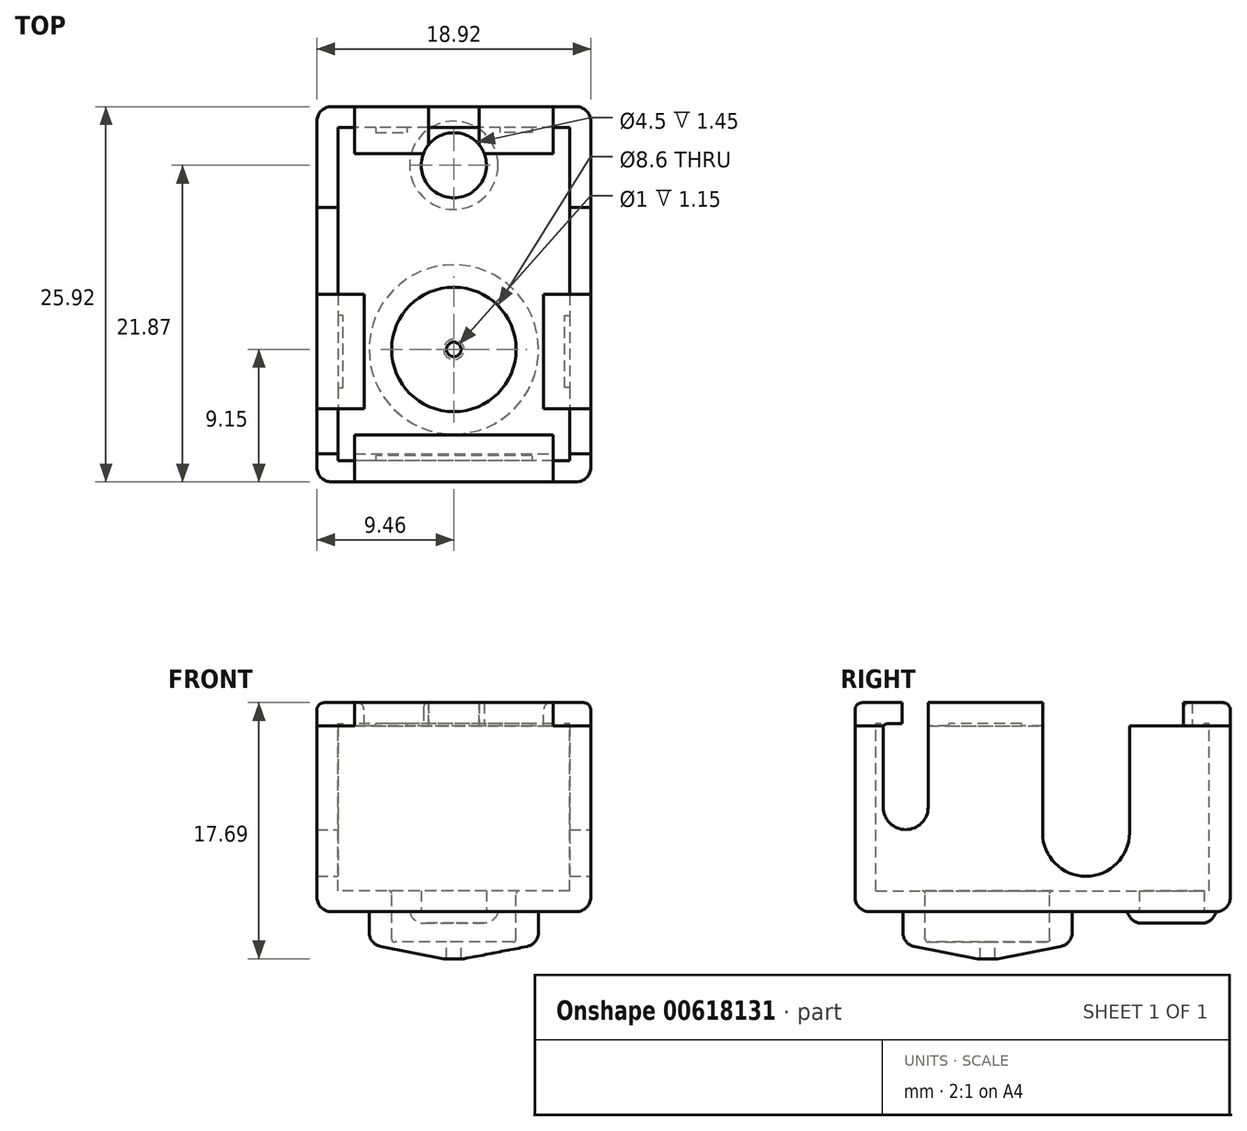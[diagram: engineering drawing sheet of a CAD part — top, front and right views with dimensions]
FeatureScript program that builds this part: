
annotation { "Feature Type Name" : "Feature", "Feature Type Description" : "" }
export const myFeature = defineFeature(function(context is Context, id is Id, definition is map)
    precondition{}
    {
        {
            var Q0;
            Q0=qCreatedBy(makeId("Top.planeOp"),FACE);
            var sketch = newSketch(context, id + "F0", { "sketchPlane" : qUnion([Q0])});
            skLineSegment(sketch, "E0.bottom", {"start": v(9.46, 12.96) * mm, "end": v(-9.45, 12.96) * mm});
            skLineSegment(sketch, "E0.top", {"start": v(9.45, -12.96) * mm, "end": v(-9.46, -12.96) * mm});
            skLineSegment(sketch, "E0.left", {"start": v(9.46, 12.96) * mm, "end": v(9.46, -12.96) * mm});
            skLineSegment(sketch, "E0.right", {"start": v(-9.45, 12.96) * mm, "end": v(-9.46, -12.96) * mm});
            skPoint(sketch, "E0.middle", {"position": v(0, 0) * mm});
            skCircle(sketch, "E1", {"center": v(0, -3.8) * mm, "radius": 5.85 * mm});
            skCircle(sketch, "E2", {"center": v(0, 8.9) * mm, "radius": 3.05 * mm});
            skCircle(sketch, "E3", {"center": v(0, -3.8) * mm, "radius": 4.3 * mm});
            skCircle(sketch, "E4", {"center": v(0, 8.9) * mm, "radius": 2.25 * mm});
            skSolve(sketch);
        }
        {
            var Q0;
            Q0=makeQuery(id+"F0.imprint","IMPRINT",FACE,{"disambiguationData":[TD([[makeQuery(id+"F0.imprint","IMPRINT",EDGE,{"derivedFrom":sQuery(id+"F0.wireOp",EDGE,"E2")}),1.0]])]});
            var Q1;
            Q1=makeQuery(id+"F0.imprint","IMPRINT",FACE,{"disambiguationData":[TD([[makeQuery(id+"F0.imprint","IMPRINT",EDGE,{"derivedFrom":sQuery(id+"F0.wireOp",EDGE,"E0.bottom")}),1.0]])]});
            var Q2;
            Q2=makeQuery(id+"F0.imprint","IMPRINT",FACE,{"disambiguationData":[TD([[makeQuery(id+"F0.imprint","IMPRINT",EDGE,{"derivedFrom":sQuery(id+"F0.wireOp",EDGE,"E1")}),1.0]])]});
            var Q3;
            Q3=makeQuery(id+"F0.imprint","IMPRINT",FACE,{"disambiguationData":[TD([[makeQuery(id+"F0.imprint","IMPRINT",EDGE,{"derivedFrom":sQuery(id+"F0.wireOp",EDGE,"E3")}),1.0]])]});
            var Q4;
            Q4=makeQuery(id+"F0.imprint","IMPRINT",FACE,{"disambiguationData":[TD([[makeQuery(id+"F0.imprint","IMPRINT",EDGE,{"derivedFrom":sQuery(id+"F0.wireOp",EDGE,"E4")}),1.0]])]});
            extrude(context, id + "F1", {"entities" : qUnion([Q0, Q1, Q2, Q3, Q4]), "depth" : (11.54 + 2 * 1.45) * mm, "offsetDistance" : 25 * mm});
        }
        {
            var Q0;
            Q0=makeQuery(id+"F1.opExtrude","SWEPT_FACE",FACE,{"disambiguationData":[OSD([sQuery(id+"F0.wireOp",EDGE,"E0.left")])]});
            var sketch = newSketch(context, id + "F2", { "sketchPlane" : qUnion([Q0])});
            skLineSegment(sketch, "E5", {"start": v(-11.01, 14.44) * mm, "end": v(-11.01, 7.22) * mm});
            skLineSegment(sketch, "E6", {"start": v(-7.9, 14.44) * mm, "end": v(-7.9, 7.22) * mm});
            skLineSegment(sketch, "E7", {"start": v(-0.01, 14.44) * mm, "end": v(-0.01, 5.45) * mm});
            skLineSegment(sketch, "E8", {"start": v(5.99, 14.44) * mm, "end": v(5.99, 5.45) * mm});
            skArc(sketch, "E9", {"start": v(-11, 7.22) * mm, "mid": v(-9.46, 5.67) * mm, "end": v(-7.9, 7.22) * mm});
            skArc(sketch, "E10", {"start": v(-0.01, 5.45) * mm, "mid": v(2.99, 2.45) * mm, "end": v(5.99, 5.45) * mm});
            skLineSegment(sketch, "E11", {"start": v(-11.01, 13) * mm, "end": v(-7.9, 13) * mm});
            skSolve(sketch);
        }
        {
            var Q0;
            Q0=makeQuery(id+"F1.opExtrude","CAP_EDGE",EDGE,{"disambiguationData":[OSD([sQuery(id+"F0.wireOp",EDGE,"E0.left")])],"isStart":true});
            var Q1;
            Q1=makeQuery(id+"F1.opExtrude","SWEPT_EDGE",EDGE,{"disambiguationData":[OSD([sQuery(id+"F0.wireOp",EDGE,"E0.bottom"),sQuery(id+"F0.wireOp",EDGE,"E0.left")])]});
            var Q2;
            Q2=makeQuery(id+"F1.opExtrude","CAP_EDGE",EDGE,{"disambiguationData":[OSD([sQuery(id+"F0.wireOp",EDGE,"E0.bottom")])],"isStart":true});
            var Q3;
            Q3=makeQuery(id+"F1.opExtrude","SWEPT_EDGE",EDGE,{"disambiguationData":[OSD([sQuery(id+"F0.wireOp",EDGE,"E0.bottom"),sQuery(id+"F0.wireOp",EDGE,"E0.right")])]});
            var Q4;
            Q4=makeQuery(id+"F1.opExtrude","CAP_EDGE",EDGE,{"disambiguationData":[OSD([sQuery(id+"F0.wireOp",EDGE,"E0.right")])],"isStart":true});
            var Q5;
            Q5=makeQuery(id+"F1.opExtrude","SWEPT_EDGE",EDGE,{"disambiguationData":[OSD([sQuery(id+"F0.wireOp",EDGE,"E0.top"),sQuery(id+"F0.wireOp",EDGE,"E0.right")])]});
            var Q6;
            Q6=makeQuery(id+"F1.opExtrude","CAP_EDGE",EDGE,{"disambiguationData":[OSD([sQuery(id+"F0.wireOp",EDGE,"E0.top")])],"isStart":true});
            var Q7;
            Q7=makeQuery(id+"F1.opExtrude","SWEPT_EDGE",EDGE,{"disambiguationData":[OSD([sQuery(id+"F0.wireOp",EDGE,"E0.top"),sQuery(id+"F0.wireOp",EDGE,"E0.left")])]});
            fillet(context, id + "F3", {"entities" : qUnion([Q0, Q1, Q2, Q3, Q4, Q5, Q6, Q7]), "radius" : 1 * mm, "tangentPropagation" : true, "allowEdgeOverflow" : false});
        }
        {
            var Q0;
            Q0=makeQuery(id+"F1.opExtrude","CAP_FACE",FACE,{"disambiguationData":[OSD([sQuery(id+"F0.wireOp",EDGE,"E0.bottom"),sQuery(id+"F0.wireOp",EDGE,"E0.top"),sQuery(id+"F0.wireOp",EDGE,"E0.left"),sQuery(id+"F0.wireOp",EDGE,"E0.right")])],"isStart":false});
            var sketch = newSketch(context, id + "F4", { "sketchPlane" : qUnion([Q0])});
            skLineSegment(sketch, "E12", {"start": v(0, -9.7) * mm, "end": v(6.86, -9.7) * mm});
            skLineSegment(sketch, "E13", {"start": v(6.86, -9.7) * mm, "end": v(6.86, -12.96) * mm});
            skLineSegment(sketch, "E14", {"start": v(9.46, -7.9) * mm, "end": v(6.2, -7.9) * mm});
            skLineSegment(sketch, "E15", {"start": v(6.2, -7.9) * mm, "end": v(6.2, -0.01) * mm});
            skLineSegment(sketch, "E16", {"start": v(6.2, -0.01) * mm, "end": v(9.46, -0.01) * mm});
            skLineSegment(sketch, "E17", {"start": v(6.86, 12.96) * mm, "end": v(6.86, 9.7) * mm});
            skLineSegment(sketch, "E18", {"start": v(6.86, 9.7) * mm, "end": v(1.76, 9.7) * mm});
            skLineSegment(sketch, "E19", {"start": v(1.76, 9.7) * mm, "end": v(1.76, 12.96) * mm});
            skLineSegment(sketch, "E20.MirrorCS", {"start": v(-6.86, 9.7) * mm, "end": v(-1.76, 9.7) * mm});
            skLineSegment(sketch, "E21.MirrorCS", {"start": v(-1.76, 9.7) * mm, "end": v(-1.76, 12.96) * mm});
            skLineSegment(sketch, "E22.MirrorCS", {"start": v(-6.86, 12.96) * mm, "end": v(-6.86, 9.7) * mm});
            skLineSegment(sketch, "E23.MirrorCS", {"start": v(-6.2, -0.01) * mm, "end": v(-9.46, -0.01) * mm});
            skLineSegment(sketch, "E24.MirrorCS", {"start": v(-6.2, -7.9) * mm, "end": v(-6.2, -0.01) * mm});
            skLineSegment(sketch, "E25.MirrorCS", {"start": v(-9.46, -7.9) * mm, "end": v(-6.2, -7.9) * mm});
            skLineSegment(sketch, "E26.MirrorCS", {"start": v(-6.86, -9.7) * mm, "end": v(-6.86, -12.96) * mm});
            skLineSegment(sketch, "E27.MirrorCS", {"start": v(0, -9.7) * mm, "end": v(-6.86, -9.7) * mm});
            skSolve(sketch);
        }
        {
            var Q0;
            Q0=makeQuery(id+"F4.imprint","IMPRINT",FACE,{"disambiguationData":[TD([[makeQuery(id+"F4.imprint","IMPRINT",EDGE,{"derivedFrom":sQuery(id+"F4.wireOp",EDGE,"E12")}),1.0]])]});
            extrude(context, id + "F5", {"entities" : qUnion([Q0]), "operationType" : NewBodyOperationType.REMOVE, "oppositeDirection" : true, "depth" : 1.6 * mm, "offsetDistance" : 25 * mm});
        }
        {
            var Q0;
            Q0=makeQuery(id+"F5.boolean.opBoolean","COPY",FACE,{"derivedFrom":makeQuery(id+"F5.opExtrude","CAP_FACE",FACE,{"disambiguationData":[OSD([sQuery(id+"F0.wireOp",EDGE,"E0.bottom"),sQuery(id+"F0.wireOp",EDGE,"E0.top"),sQuery(id+"F0.wireOp",EDGE,"E0.left"),sQuery(id+"F0.wireOp",EDGE,"E0.right"),sQuery(id+"F4.wireOp",EDGE,"E12"),sQuery(id+"F4.wireOp",EDGE,"E13"),sQuery(id+"F4.wireOp",EDGE,"E14"),sQuery(id+"F4.wireOp",EDGE,"E15"),sQuery(id+"F4.wireOp",EDGE,"E16"),sQuery(id+"F4.wireOp",EDGE,"E17"),sQuery(id+"F4.wireOp",EDGE,"E18"),sQuery(id+"F4.wireOp",EDGE,"E19"),sQuery(id+"F4.wireOp",EDGE,"E20.MirrorCS"),sQuery(id+"F4.wireOp",EDGE,"E21.MirrorCS"),sQuery(id+"F4.wireOp",EDGE,"E22.MirrorCS"),sQuery(id+"F4.wireOp",EDGE,"E23.MirrorCS"),sQuery(id+"F4.wireOp",EDGE,"E24.MirrorCS"),sQuery(id+"F4.wireOp",EDGE,"E25.MirrorCS"),sQuery(id+"F4.wireOp",EDGE,"E26.MirrorCS"),sQuery(id+"F4.wireOp",EDGE,"E27.MirrorCS")])],"isStart":false})});
            shell(context, id + "F6", {"entities" : qUnion([Q0]), "thickness" : 1.45 * mm});
        }
        {
            var Q0;
            Q0=makeQuery(id+"F0.imprint","IMPRINT",FACE,{"disambiguationData":[TD([[makeQuery(id+"F0.imprint","IMPRINT",EDGE,{"derivedFrom":sQuery(id+"F0.wireOp",EDGE,"E2")}),1.0]])]});
            var Q1;
            Q1=makeQuery(id+"F0.imprint","IMPRINT",FACE,{"disambiguationData":[TD([[makeQuery(id+"F0.imprint","IMPRINT",EDGE,{"derivedFrom":sQuery(id+"F0.wireOp",EDGE,"E4")}),1.0]])]});
            extrude(context, id + "F7", {"entities" : qUnion([Q0, Q1]), "operationType" : NewBodyOperationType.ADD, "oppositeDirection" : true, "depth" : 0.8 * mm, "offsetDistance" : 25 * mm});
        }
        {
            var Q0;
            Q0=makeQuery(id+"F7.opExtrude","CAP_EDGE",EDGE,{"disambiguationData":[OSD([sQuery(id+"F0.wireOp",EDGE,"E2")])],"isStart":false});
            fillet(context, id + "F8", {"entities" : qUnion([Q0]), "radius" : 1 * mm, "tangentPropagation" : true, "allowEdgeOverflow" : false});
        }
        {
            var Q0;
            Q0=makeQuery(id+"F0.imprint","IMPRINT",FACE,{"disambiguationData":[TD([[makeQuery(id+"F0.imprint","IMPRINT",EDGE,{"derivedFrom":sQuery(id+"F0.wireOp",EDGE,"E1")}),1.0]])]});
            var Q1;
            Q1=makeQuery(id+"F0.imprint","IMPRINT",FACE,{"disambiguationData":[TD([[makeQuery(id+"F0.imprint","IMPRINT",EDGE,{"derivedFrom":sQuery(id+"F0.wireOp",EDGE,"E3")}),1.0]])]});
            extrude(context, id + "F9", {"entities" : qUnion([Q0, Q1]), "operationType" : NewBodyOperationType.ADD, "oppositeDirection" : true, "depth" : 3.25 * mm, "offsetDistance" : 25 * mm});
        }
        {
            var Q0;
            Q0=makeQuery(id+"F9.opExtrude","CAP_EDGE",EDGE,{"disambiguationData":[OSD([sQuery(id+"F0.wireOp",EDGE,"E1")])],"isStart":false});
            chamfer(context, id + "F10", {"entities" : qUnion([Q0]), "chamferType" : ChamferType.OFFSET_ANGLE, "width" : 1 * mm, "oppositeDirection" : false, "angle" : 79 * degree, "tangentPropagation" : true});
        }
        {
            var Q0;
            Q0=makeQuery(id+"F9.opExtrude","CAP_EDGE",EDGE,{"disambiguationData":[OSD([sQuery(id+"F0.wireOp",EDGE,"E1")])],"isStart":true});
            var Q1;
            {var subQ0=sQuery(id+"F0.wireOp",EDGE,"E1");Q1=makeQuery(id+"F10.opChamfer","BLEND_EDGE",EDGE,{"blendedFrom":[makeQuery(id+"F9.opExtrude","CAP_EDGE",EDGE,{"disambiguationData":[OSD([subQ0])],"isStart":false}),makeQuery(id+"F9.opExtrude","SWEPT_FACE",FACE,{"disambiguationData":[OSD([subQ0])]})],"blendedInto":[makeQuery(id+"F9.opExtrude","SWEPT_FACE",FACE,{"disambiguationData":[OSD([subQ0])]})]});}
            fillet(context, id + "F11", {"entities" : qUnion([Q0, Q1]), "radius" : 1 * mm, "tangentPropagation" : true, "allowEdgeOverflow" : false});
        }
        {
            var Q0;
            Q0=makeQuery(id+"F0.imprint","IMPRINT",FACE,{"disambiguationData":[TD([[makeQuery(id+"F0.imprint","IMPRINT",EDGE,{"derivedFrom":sQuery(id+"F0.wireOp",EDGE,"E3")}),1.0]])]});
            extrude(context, id + "F12", {"entities" : qUnion([Q0]), "operationType" : NewBodyOperationType.REMOVE, "oppositeDirection" : true, "depth" : 2.1 * mm, "offsetDistance" : 25 * mm});
        }
        {
            var Q0;
            Q0=makeQuery(id+"F0.imprint","IMPRINT",FACE,{"disambiguationData":[TD([[makeQuery(id+"F0.imprint","IMPRINT",EDGE,{"derivedFrom":sQuery(id+"F0.wireOp",EDGE,"E3")}),1.0]])]});
            var Q1;
            Q1=makeQuery(id+"F0.imprint","IMPRINT",FACE,{"disambiguationData":[TD([[makeQuery(id+"F0.imprint","IMPRINT",EDGE,{"derivedFrom":sQuery(id+"F0.wireOp",EDGE,"E4")}),1.0]])]});
            extrude(context, id + "F13", {"entities" : qUnion([Q0, Q1]), "operationType" : NewBodyOperationType.REMOVE, "endBound" : BoundingType.THROUGH_ALL, "depth" : 25 * mm, "offsetDistance" : 25 * mm});
        }
        {
            var Q0;
            Q0=sQuery(id+"F0.wireOp",VERTEX,"E1.center");
            var Q1;
            Q1=makeQuery(id+"F1.opExtrude","SWEPT_BODY",BODY,{"disambiguationData":[OSD([sQuery(id+"F0.wireOp",EDGE,"E0.bottom"),sQuery(id+"F0.wireOp",EDGE,"E0.top"),sQuery(id+"F0.wireOp",EDGE,"E0.left"),sQuery(id+"F0.wireOp",EDGE,"E0.right")])]});
            hole(context, id + "F14", {"style" : HoleStyle.SIMPLE, "endStyle" : HoleEndStyle.BLIND, "holeDiameter" : 1 * mm, "majorDiameter" : 5 * mm, "holeDepth" : 1.4 * mm, "isTappedThrough" : true, "tappedDepth" : 12 * mm, "tapClearance" : 3, "locations" : qUnion([Q0]), "scope" : qUnion([Q1])});
        }
        {
            var Q0;
            Q0=makeQuery(id+"F13.boolean.opBoolean","INTERSECT",EDGE,{"derivedFrom":[makeQuery(id+"F6.opShell","OFFSET_FACE",FACE,{"disambiguationData":[OSD([sQuery(id+"F0.wireOp",EDGE,"E0.bottom"),sQuery(id+"F0.wireOp",EDGE,"E0.top"),sQuery(id+"F0.wireOp",EDGE,"E0.left"),sQuery(id+"F0.wireOp",EDGE,"E0.right")])]}),makeQuery(id+"F13.opExtrude","SWEPT_FACE",FACE,{"disambiguationData":[OSD([sQuery(id+"F0.wireOp",EDGE,"E3")])]})]});
            var Q1;
            Q1=makeQuery(id+"F12.boolean.opBoolean","COPY",EDGE,{"derivedFrom":makeQuery(id+"F12.opExtrude","CAP_EDGE",EDGE,{"disambiguationData":[OSD([sQuery(id+"F0.wireOp",EDGE,"E3")])],"isStart":false})});
            fillet(context, id + "F15", {"entities" : qUnion([Q0, Q1]), "radius" : 0.2 * mm, "tangentPropagation" : true, "allowEdgeOverflow" : false});
        }
        {
            var Q0;
            {var subQ0=sQuery(id+"F2.wireOp",EDGE,"E9");Q0=makeQuery(id+"F2.imprint","IMPRINT",FACE,{"disambiguationData":[TD([[makeQuery(id+"F2.imprint","IMPRINT",EDGE,{"derivedFrom":subQ0}),1.0]])]});}
            var Q1;
            {var subQ0=sQuery(id+"F2.wireOp",EDGE,"E7");Q1=makeQuery(id+"F2.imprint","IMPRINT",FACE,{"disambiguationData":[TD([[makeQuery(id+"F2.imprint","IMPRINT",EDGE,{"derivedFrom":subQ0}),1.0]])]});}
            extrude(context, id + "F16", {"entities" : qUnion([Q0, Q1]), "operationType" : NewBodyOperationType.REMOVE, "endBound" : BoundingType.THROUGH_ALL, "oppositeDirection" : true, "depth" : 25 * mm, "offsetDistance" : 25 * mm});
        }
        {
            var Q0;
            Q0=makeQuery(id+"F1.opExtrude","CAP_EDGE",EDGE,{"disambiguationData":[OSD([sQuery(id+"F0.wireOp",EDGE,"E0.top")])],"isStart":false});
            var Q1;
            Q1=makeQuery(id+"F16.boolean.opBoolean","COPY",EDGE,{"derivedFrom":makeQuery(id+"F16.opExtrude","SWEPT_EDGE",EDGE,{"disambiguationData":[OSD([sQuery(id+"F0.wireOp",EDGE,"E0.left"),sQuery(id+"F2.wireOp",EDGE,"E5")])]})});
            var Q2;
            Q2=makeQuery(id+"F1.opExtrude","CAP_EDGE",EDGE,{"disambiguationData":[OSD([sQuery(id+"F0.wireOp",EDGE,"E0.left")])],"isStart":false});
            var Q3;
            Q3=makeQuery(id+"F5.boolean.opBoolean","COPY",EDGE,{"derivedFrom":makeQuery(id+"F5.opExtrude","CAP_EDGE",EDGE,{"disambiguationData":[OSD([sQuery(id+"F4.wireOp",EDGE,"E15")])],"isStart":true})});
            var Q4;
            Q4=makeQuery(id+"F5.boolean.opBoolean","COPY",EDGE,{"derivedFrom":makeQuery(id+"F5.opExtrude","CAP_EDGE",EDGE,{"disambiguationData":[OSD([sQuery(id+"F4.wireOp",EDGE,"E24.MirrorCS")])],"isStart":true})});
            var Q5;
            Q5=makeQuery(id+"F1.opExtrude","CAP_EDGE",EDGE,{"disambiguationData":[OSD([sQuery(id+"F0.wireOp",EDGE,"E0.right")])],"isStart":false});
            var Q6;
            {var subQ0=sQuery(id+"F0.wireOp",EDGE,"E0.bottom");Q6=makeQuery(id+"F5.boolean.opBoolean","SPLIT",EDGE,{"disambiguationData":[TD([makeQuery(id+"F5.opExtrude","SWEPT_FACE",FACE,{"disambiguationData":[OSD([sQuery(id+"F4.wireOp",EDGE,"E17")])]})])],"derivedFrom":makeQuery(id+"F1.opExtrude","CAP_EDGE",EDGE,{"disambiguationData":[OSD([subQ0])],"isStart":false})});}
            var Q7;
            {var subQ0=sQuery(id+"F0.wireOp",EDGE,"E0.bottom");Q7=makeQuery(id+"F5.boolean.opBoolean","SPLIT",EDGE,{"disambiguationData":[TD([makeQuery(id+"F5.opExtrude","SWEPT_FACE",FACE,{"disambiguationData":[OSD([sQuery(id+"F4.wireOp",EDGE,"E21.MirrorCS")])]})])],"derivedFrom":makeQuery(id+"F1.opExtrude","CAP_EDGE",EDGE,{"disambiguationData":[OSD([subQ0])],"isStart":false})});}
            var Q8;
            Q8=makeQuery(id+"F5.boolean.opBoolean","COPY",EDGE,{"derivedFrom":makeQuery(id+"F5.opExtrude","CAP_EDGE",EDGE,{"disambiguationData":[OSD([sQuery(id+"F4.wireOp",EDGE,"E20.MirrorCS")])],"isStart":true})});
            var Q9;
            Q9=makeQuery(id+"F5.boolean.opBoolean","COPY",EDGE,{"derivedFrom":makeQuery(id+"F5.opExtrude","CAP_EDGE",EDGE,{"disambiguationData":[OSD([sQuery(id+"F4.wireOp",EDGE,"E18")])],"isStart":true})});
            fillet(context, id + "F17", {"entities" : qUnion([Q0, Q1, Q2, Q3, Q4, Q5, Q6, Q7, Q8, Q9]), "radius" : 0.5 * mm, "tangentPropagation" : true, "allowEdgeOverflow" : false});
        }
    });
